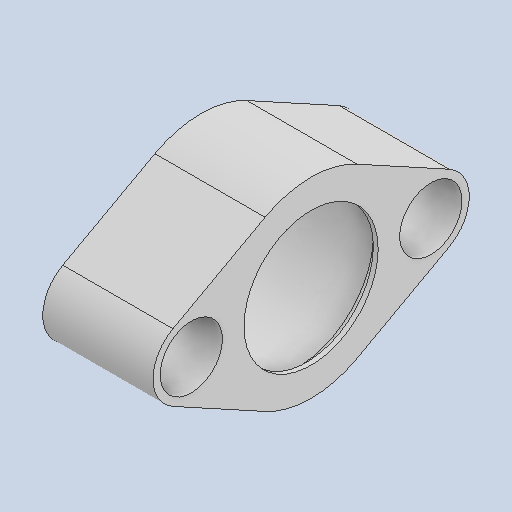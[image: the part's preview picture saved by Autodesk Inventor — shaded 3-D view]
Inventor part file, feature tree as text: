
AUTODESK INVENTOR PART (.ipt)
format: ipt  version: 2022 (Build 260153000, 153)  size: 165,376 bytes
history: native  units: in
note: dims shown in document units (in); Inventor stores cm internally (conversion verified against a paired STEP export)
features: sketch x5, hole x2, chamfer x2, plane x1, extrude x1
ambient origin geometry x8: Origin, YZ Plane, XZ Plane, XY Plane, X Axis, Y Axis, Z Axis, Center Point
bodies: Body1 (feature_tree)
feature tree (11):
  plane  "Work Plane1"
  extrude  "Extrusion1"  Depth=0.4528in TaperAngle=0.0deg
  hole  "Hole2"  [1 undecoded]
  hole  "Hole1"  [1 undecoded]
  chamfer  "Chamfer2"  Distance=0.0197in
  chamfer  "Chamfer1"  Distance=0.0394in
  sketch  "Sketch1"  dims[d0=-0.3937in d1=0.4528in d2=0.0in]
  sketch  "Sketch2"  dims[d3=0.5512in d4=0.2362in d5=0.1575in d6=0.0787in d7=90.0deg d8=0.315in d9=0.8108in]
  sketch  "Sketch3"  dims[d10=0.126in d11=0.2362in d12=0.2559in d13=0.2362in d14=90.0deg d15=0.315in d16=0.0in]
  sketch  "Sketch4"  dims[d17=0.126in d18=0.2362in d19=0.2559in d20=0.2362in d21=90.0deg d22=0.315in d23=0.0in]
  sketch  "Sketch5"  dims[d24=0.6299in d25=0.2362in d26=0.1575in d27=0.0787in d28=90.0deg d29=0.3937in d30=0.6184in d31=0.0197in d32=0.0197in d33=17.7165in d34=0.0197in d35=0.0197in d36=17.7165in d37=0.0197in d38=0.0197in d39=17.7165in d40=0.0394in d41=0.0394in d42=0.0394in d43=0.0059in d44=0.0098in d45=0.0148in d46=32.2835in d47=0.0295in d48=46.4567in d49=0.0025in d50=0.0295in d51=0.0148in]
note: 2 required parameter values undecoded (feature->parameter linkage not recoverable at this tier; creation-order binding heuristic only, values carry confidence <= 0.55)
